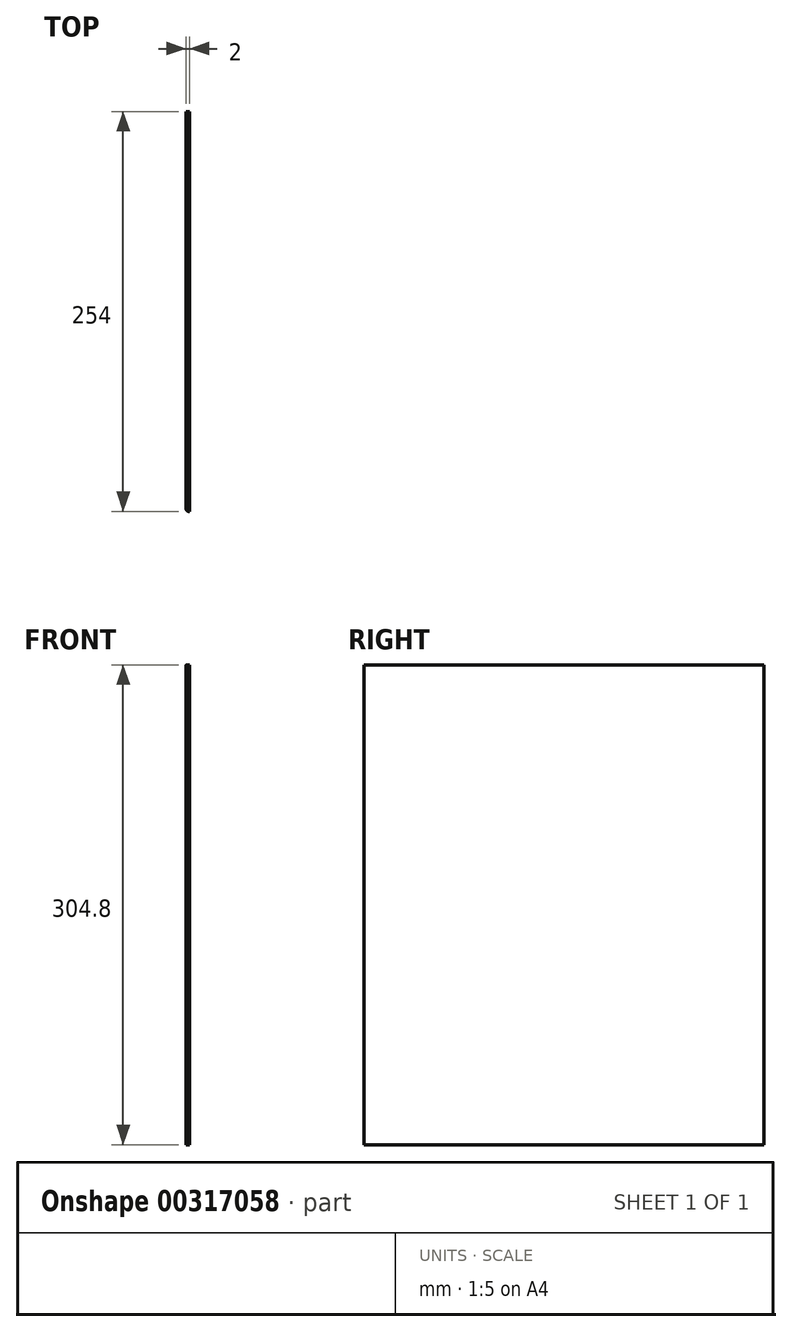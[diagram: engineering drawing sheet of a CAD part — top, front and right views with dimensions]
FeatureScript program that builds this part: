
annotation { "Feature Type Name" : "Feature", "Feature Type Description" : "" }
export const myFeature = defineFeature(function(context is Context, id is Id, definition is map)
    precondition{}
    {
        {
            var Q0;
            Q0=qCreatedBy(makeId("Right.planeOp"),FACE);
            var sketch = newSketch(context, id + "F0", { "sketchPlane" : qUnion([Q0])});
            skLineSegment(sketch, "E0.bottom", {"start": v(0, 0) * mm, "end": v(254, 0) * mm});
            skLineSegment(sketch, "E0.top", {"start": v(0, 304.8) * mm, "end": v(254, 304.8) * mm});
            skLineSegment(sketch, "E0.left", {"start": v(0, 0) * mm, "end": v(0, 304.8) * mm});
            skLineSegment(sketch, "E0.right", {"start": v(254, 0) * mm, "end": v(254, 304.8) * mm});
            skSolve(sketch);
        }
        {
            var Q0;
            Q0=makeQuery(id+"F0.imprint","IMPRINT",FACE,{"disambiguationData":[TD([[makeQuery(id+"F0.imprint","IMPRINT",EDGE,{"derivedFrom":sQuery(id+"F0.wireOp",EDGE,"E0.bottom")}),1.0]])]});
            extrude(context, id + "F1", {"entities" : qUnion([Q0]), "depth" : 2 * mm});
        }
        {
            var Q0;
            Q0=makeQuery(id+"F1.opExtrude","CAP_EDGE",EDGE,{"disambiguationData":[OSD([sQuery(id+"F0.wireOp",EDGE,"E0.left")])],"isStart":true});
            fillet(context, id + "F2", {"entities" : qUnion([Q0]), "radius" : 1.27 * mm, "tangentPropagation" : true, "allowEdgeOverflow" : false});
        }
    });
